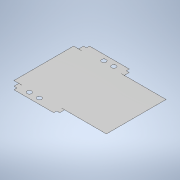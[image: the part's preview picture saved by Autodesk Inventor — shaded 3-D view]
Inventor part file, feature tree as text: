
AUTODESK INVENTOR PART (.ipt)
format: ipt  version: 2022 (Build 260153000, 153)  size: 222,720 bytes
history: native  units: in
note: dims shown in document units (in); Inventor stores cm internally (conversion verified against a paired STEP export)
features: extrude x5, sketch x5
ambient origin geometry x8: Origin, YZ Plane, XZ Plane, XY Plane, X Axis, Y Axis, Z Axis, Center Point
bodies: Body1 (feature_tree)
feature tree (10):
  extrude  "Extrusion1"  Depth=29.9213in
  extrude  "Extrusion4"  Depth=3.1496in
  extrude  "Extrusion5"  Depth=15.748in
  extrude  "Extrusion6"  Depth=3.1496in
  extrude  "Extrusion7"  Depth=1.1811in
  sketch  "Sketch1"  dims[d0=36.6142in d1=29.9213in]
  sketch  "Sketch5"  dims[d2=0.0039in d3=0.0in d33=3.1496in]
  sketch  "Sketch6"  dims[d34=3.1496in d35=15.748in]
  sketch  "Sketch7"  dims[d36=15.748in d37=3.1496in]
  sketch  "Sketch8"  dims[d38=3.1496in d39=1.1811in d40=0.0in d41=0.0in d42=1.1811in d43=1.1811in d44=3.1496in d45=0.7874in d46=1.1811in d47=1.1811in d48=0.7874in d49=0.7874in d50=1.1811in d51=1.1811in d52=3.1496in d53=0.7874in d54=1.1811in d55=1.1811in d56=0.0in d57=0.0in d58=1.7717in d59=1.7717in d60=0.9843in d61=3.937in d62=7.874in d63=1.7717in d64=1.7717in d65=0.9843in d66=3.937in d67=7.874in d68=0.3937in d69=0.0in d70=1.1811in d72=0.0079in d74=1.1811in d75=0.0079in d76=0.0079in d77=1.1811in d78=0.0079in d79=1.1811in d80=0.0in d81=0.0in]
